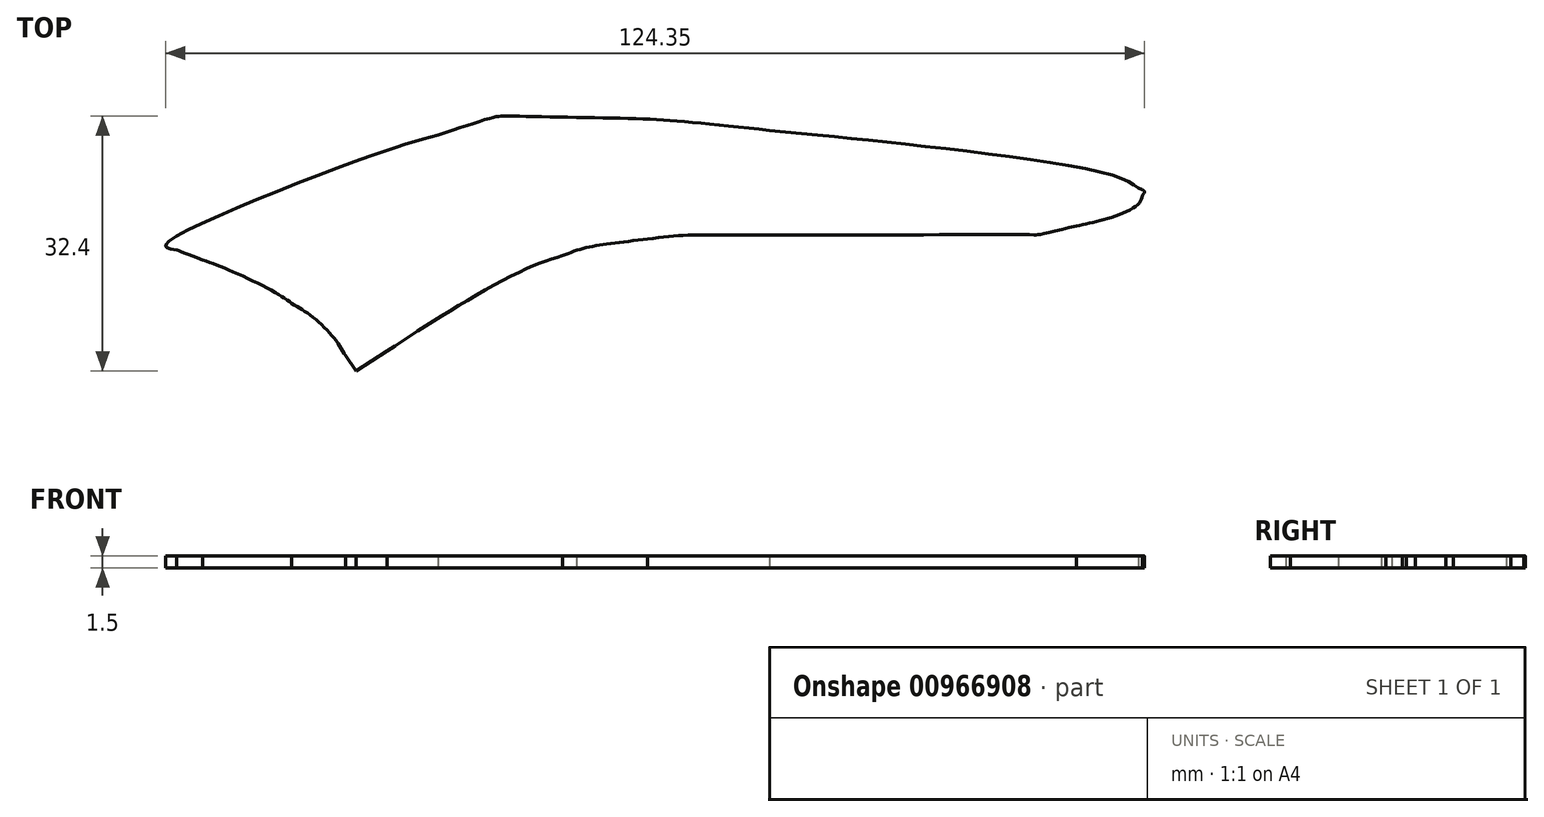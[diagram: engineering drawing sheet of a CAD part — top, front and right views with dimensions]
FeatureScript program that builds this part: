
annotation { "Feature Type Name" : "Feature", "Feature Type Description" : "" }
export const myFeature = defineFeature(function(context is Context, id is Id, definition is map)
    precondition{}
    {
        {
            var Q0;
            Q0=qCreatedBy(makeId("Top.planeOp"),FACE);
            var sketch = newSketch(context, id + "F0", { "sketchPlane" : qUnion([Q0])});
            skLineSegment(sketch, "E0", {"start": v(66, -18.03) * mm, "end": v(64.28, -18.58) * mm});
            skLineSegment(sketch, "E1", {"start": v(64.28, -18.58) * mm, "end": v(66.47, -18.74) * mm});
            skLineSegment(sketch, "E2", {"start": v(70.08, -28) * mm, "end": v(70, -33.38) * mm});
            skLineSegment(sketch, "E3", {"start": v(70, -33.38) * mm, "end": v(69.08, -32.29) * mm});
            skLineSegment(sketch, "E4", {"start": v(8.94, -2.25) * mm, "end": v(8.28, -1.7) * mm});
            skLineSegment(sketch, "E5", {"start": v(8.28, -1.7) * mm, "end": v(11.28, -0.13) * mm});
            skLineSegment(sketch, "E6", {"start": v(-43.45, -6.77) * mm, "end": v(-49.68, -8.05) * mm});
            skLineSegment(sketch, "E7", {"start": v(-49.68, -8.05) * mm, "end": v(-50.6, -8.32) * mm});
            skLineSegment(sketch, "E8", {"start": v(-50.6, -8.32) * mm, "end": v(-43.45, -6.77) * mm});
            skLineSegment(sketch, "E9", {"start": v(72.43, 4.75) * mm, "end": v(68.45, 2.21) * mm});
            skLineSegment(sketch, "E10", {"start": v(68.45, 2.21) * mm, "end": v(67.15, 4.16) * mm});
            skFitSpline(sketch, "E11", {"points": [v(-57.67, 34.81) * mm, v(-61.28, 35.6) * mm, v(-64.27, 36.27) * mm, v(-64.32, 36.32) * mm]});
            skFitSpline(sketch, "E12", {"points": [v(-64.32, 36.32) * mm, v(-64.37, 36.37) * mm, v(-62.06, 37.36) * mm, v(-59.2, 38.5) * mm]});
            skFitSpline(sketch, "E13", {"points": [v(-59.2, 38.5) * mm, v(-52.7, 41.11) * mm, v(-45.06, 44.34) * mm, v(-37.82, 47.53) * mm]});
            skFitSpline(sketch, "E14", {"points": [v(-37.82, 47.53) * mm, v(-34.77, 48.88) * mm, v(-32.09, 49.98) * mm, v(-31.87, 49.98) * mm]});
            skFitSpline(sketch, "E15", {"points": [v(-31.87, 49.98) * mm, v(-31.65, 49.98) * mm, v(-29.02, 47.85) * mm, v(-26.02, 45.24) * mm]});
            skFitSpline(sketch, "E16", {"points": [v(-26.02, 45.24) * mm, v(-10.46, 31.7) * mm, v(-3.56, 27.4) * mm, v(4.58, 26.18) * mm]});
            skFitSpline(sketch, "E17", {"points": [v(4.58, 26.18) * mm, v(6.3, 25.93) * mm, v(10.11, 25.84) * mm, v(17.52, 25.9) * mm]});
            skFitSpline(sketch, "E18", {"points": [v(17.52, 25.9) * mm, v(24.34, 25.94) * mm, v(28.65, 25.85) * mm, v(29.83, 25.64) * mm]});
            skFitSpline(sketch, "E19", {"points": [v(29.83, 25.64) * mm, v(32.66, 25.14) * mm, v(35.57, 23.55) * mm, v(38.21, 21.06) * mm]});
            skFitSpline(sketch, "E20", {"points": [v(38.21, 21.06) * mm, v(41.5, 17.97) * mm, v(42.57, 17.32) * mm, v(48.6, 14.74) * mm]});
            skFitSpline(sketch, "E21", {"points": [v(48.6, 14.74) * mm, v(56.67, 11.29) * mm, v(60.17, 9.25) * mm, v(63.53, 6.05) * mm]});
            skFitSpline(sketch, "E22", {"points": [v(63.53, 6.05) * mm, v(68.07, 1.72) * mm, v(70.15, -3.63) * mm, v(69.77, -10) * mm]});
            skFitSpline(sketch, "E23", {"points": [v(69.77, -10) * mm, v(69.6, -13) * mm, v(68.77, -16.55) * mm, v(68.1, -17.14) * mm]});
            skFitSpline(sketch, "E24", {"points": [v(68.1, -17.14) * mm, v(67.9, -17.33) * mm, v(66.95, -17.73) * mm, v(66, -18.03) * mm]});
            skFitSpline(sketch, "E25", {"points": [v(66.47, -18.74) * mm, v(67.68, -18.83) * mm, v(68.86, -19.07) * mm, v(69.1, -19.27) * mm]});
            skFitSpline(sketch, "E26", {"points": [v(69.1, -19.27) * mm, v(69.87, -19.9) * mm, v(70.14, -22.4) * mm, v(70.08, -28) * mm]});
            skFitSpline(sketch, "E27", {"points": [v(69.08, -32.29) * mm, v(68.23, -31.3) * mm, v(66.27, -28.58) * mm, v(61.42, -21.65) * mm]});
            skFitSpline(sketch, "E28", {"points": [v(61.42, -21.65) * mm, v(59.43, -18.8) * mm, v(56.75, -15.85) * mm, v(55.45, -15.05) * mm]});
            skFitSpline(sketch, "E29", {"points": [v(55.45, -15.05) * mm, v(54.15, -14.25) * mm, v(52.09, -13.78) * mm, v(43.38, -12.3) * mm]});
            skFitSpline(sketch, "E30", {"points": [v(43.38, -12.3) * mm, v(31.49, -10.27) * mm, v(24.3, -8.65) * mm, v(18.52, -6.7) * mm]});
            skFitSpline(sketch, "E31", {"points": [v(18.52, -6.7) * mm, v(15.59, -5.7) * mm, v(9.94, -3.08) * mm, v(8.94, -2.25) * mm]});
            skFitSpline(sketch, "E32", {"points": [v(11.28, -0.13) * mm, v(12.93, 0.74) * mm, v(14.17, 1.49) * mm, v(14.04, 1.54) * mm]});
            skFitSpline(sketch, "E33", {"points": [v(14.04, 1.54) * mm, v(13.76, 1.63) * mm, v(8.22, 0.96) * mm, v(-3.3, -0.58) * mm]});
            skFitSpline(sketch, "E34", {"points": [v(-3.3, -0.58) * mm, v(-21.42, -3) * mm, v(-34.35, -4.92) * mm, v(-43.45, -6.77) * mm]});
            skFitSpline(sketch, "E35", {"points": [v(-50.6, -8.32) * mm, v(-53.64, -9.02) * mm, v(-61.83, -12.62) * mm, v(-78.88, -20.74) * mm]});
            skFitSpline(sketch, "E36", {"points": [v(-78.88, -20.74) * mm, v(-104.14, -32.77) * mm, v(-118.17, -38.13) * mm, v(-127.65, -39.4) * mm]});
            skFitSpline(sketch, "E37", {"points": [v(-127.65, -39.4) * mm, v(-130.38, -39.76) * mm, v(-131.55, -39.62) * mm, v(-131.83, -38.9) * mm]});
            skFitSpline(sketch, "E38", {"points": [v(-131.83, -38.9) * mm, v(-132.16, -38.03) * mm, v(-130.9, -35.95) * mm, v(-128.6, -33.55) * mm]});
            skFitSpline(sketch, "E39", {"points": [v(-128.6, -33.55) * mm, v(-126.35, -31.2) * mm, v(-116.88, -23.42) * mm, v(-116.81, -23.36) * mm, v(-116.81, -23.36) * mm, v(-116.81, -23.36) * mm]});
            skFitSpline(sketch, "E40", {"points": [v(-116.81, -23.36) * mm, v(-116.81, -23.36) * mm, v(-116.81, -23.36) * mm, v(-116.76, -23.32) * mm, v(-108.8, -16.53) * mm, v(-99.79, -8.13) * mm]});
            skFitSpline(sketch, "E41", {"points": [v(-99.79, -8.13) * mm, v(-86.44, 4.3) * mm, v(-82.66, 7.05) * mm, v(-76.4, 8.86) * mm]});
            skFitSpline(sketch, "E42", {"points": [v(-76.4, 8.86) * mm, v(-71.61, 10.24) * mm, v(-64.73, 11.31) * mm, v(-55.89, 12.04) * mm]});
            skFitSpline(sketch, "E43", {"points": [v(-55.89, 12.04) * mm, v(-53, 12.28) * mm, v(-50.46, 12.47) * mm, v(-49.88, 12.45) * mm]});
            skFitSpline(sketch, "E44", {"points": [v(-49.88, 12.45) * mm, v(-49.54, 12.45) * mm, v(-47.77, 12.6) * mm, v(-47.75, 12.6) * mm, v(-47.75, 12.6) * mm, v(-47.75, 12.6) * mm]});
            skFitSpline(sketch, "E45", {"points": [v(-47.75, 12.6) * mm, v(-46.76, 12.69) * mm, v(-42.74, 12.96) * mm, v(-38.8, 13.2) * mm]});
            skFitSpline(sketch, "E46", {"points": [v(-38.8, 13.2) * mm, v(-28.29, 13.84) * mm, v(-20.91, 14.57) * mm, v(-15.6, 15.48) * mm]});
            skFitSpline(sketch, "E47", {"points": [v(-15.6, 15.48) * mm, v(-12.64, 16) * mm, v(-7.7, 17.26) * mm, v(-7.37, 17.59) * mm]});
            skFitSpline(sketch, "E48", {"points": [v(-7.37, 17.59) * mm, v(-7.25, 17.7) * mm, v(-8.73, 18.04) * mm, v(-10.66, 18.32) * mm]});
            skFitSpline(sketch, "E49", {"points": [v(-10.66, 18.32) * mm, v(-15.43, 19) * mm, v(-15.3, 18.96) * mm, v(-16, 20.2) * mm]});
            skFitSpline(sketch, "E50", {"points": [v(-16, 20.2) * mm, v(-16.8, 21.64) * mm, v(-18, 22.67) * mm, v(-20.94, 24.42) * mm]});
            skFitSpline(sketch, "E51", {"points": [v(-20.94, 24.42) * mm, v(-24.93, 26.82) * mm, v(-30.42, 28.6) * mm, v(-42.8, 31.5) * mm]});
            skFitSpline(sketch, "E52", {"points": [v(-42.8, 31.5) * mm, v(-45.96, 32.23) * mm, v(-48.76, 32.9) * mm, v(-49.95, 33.13) * mm]});
            skFitSpline(sketch, "E53", {"points": [v(-49.95, 33.13) * mm, v(-50.82, 33.32) * mm, v(-54.06, 34.03) * mm, v(-57.67, 34.81) * mm]});
            skFitSpline(sketch, "E54", {"points": [v(45.67, 17.61) * mm, v(44.27, 18.2) * mm, v(68.87, 29.02) * mm, v(78.87, 32.2) * mm]});
            skFitSpline(sketch, "E55", {"points": [v(78.87, 32.2) * mm, v(85.87, 34.44) * mm, v(87.2, 34.6) * mm, v(96.5, 34.42) * mm]});
            skFitSpline(sketch, "E56", {"points": [v(96.5, 34.42) * mm, v(104.69, 34.26) * mm, v(110.33, 33.89) * mm, v(120.98, 32.79) * mm]});
            skFitSpline(sketch, "E57", {"points": [v(120.98, 32.79) * mm, v(141.46, 30.67) * mm, v(164.79, 27.02) * mm, v(167.87, 25.46) * mm]});
            skFitSpline(sketch, "E58", {"points": [v(167.87, 25.46) * mm, v(168.53, 25.12) * mm, v(168.61, 24.96) * mm, v(168.37, 24.5) * mm]});
            skFitSpline(sketch, "E59", {"points": [v(168.37, 24.5) * mm, v(167.75, 23.34) * mm, v(163.82, 21.55) * mm, v(159.95, 20.65) * mm]});
            skFitSpline(sketch, "E60", {"points": [v(159.95, 20.65) * mm, v(155.17, 19.54) * mm, v(154.63, 19.52) * mm, v(131.86, 19.5) * mm]});
            skFitSpline(sketch, "E61", {"points": [v(131.86, 19.5) * mm, v(112.6, 19.48) * mm, v(108.97, 19.4) * mm, v(105.52, 18.98) * mm]});
            skFitSpline(sketch, "E62", {"points": [v(105.52, 18.98) * mm, v(100.08, 18.32) * mm, v(97.13, 17.74) * mm, v(94.69, 16.86) * mm]});
            skFitSpline(sketch, "E63", {"points": [v(94.69, 16.86) * mm, v(90.38, 15.32) * mm, v(80.96, 10.2) * mm, v(72.43, 4.75) * mm]});
            skFitSpline(sketch, "E64", {"points": [v(67.15, 4.16) * mm, v(65.66, 6.4) * mm, v(62.79, 9.2) * mm, v(60.3, 10.82) * mm]});
            skFitSpline(sketch, "E65", {"points": [v(60.3, 10.82) * mm, v(58.11, 12.24) * mm, v(52.53, 14.95) * mm, v(48.96, 16.33) * mm]});
            skFitSpline(sketch, "E66", {"points": [v(48.96, 16.33) * mm, v(47.47, 16.9) * mm, v(45.99, 17.48) * mm, v(45.67, 17.61) * mm]});
            skCircle(sketch, "E67", {"center": v(53.12, -6.56) * mm, "radius": 1.41 * mm});
            skSolve(sketch);
        }
        {
            var Q0;
            Q0=makeQuery(id+"F0.imprint","IMPRINT",FACE,{"disambiguationData":[TD([[makeQuery(id+"F0.imprint","IMPRINT",EDGE,{"derivedFrom":sQuery(id+"F0.wireOp",EDGE,"E0")}),-1.0]])]});
            var Q1;
            Q1=makeQuery(id+"F0.imprint","IMPRINT",FACE,{"disambiguationData":[TD([[makeQuery(id+"F0.imprint","IMPRINT",EDGE,{"derivedFrom":sQuery(id+"F0.wireOp",EDGE,"1a79e27b-043b-4259-81ca-ee435dd8310d")}),1.0]])]});
            var Q2;
            Q2=makeQuery(id+"F0.imprint","IMPRINT",FACE,{"disambiguationData":[TD([[makeQuery(id+"F0.imprint","IMPRINT",EDGE,{"derivedFrom":sQuery(id+"F0.wireOp",EDGE,"E9")}),-1.0]])]});
            extrude(context, id + "F1", {"entities" : qUnion([Q0, Q1, Q2]), "depth" : 1.5 * mm, "offsetDistance" : 25 * mm});
        }
    });
